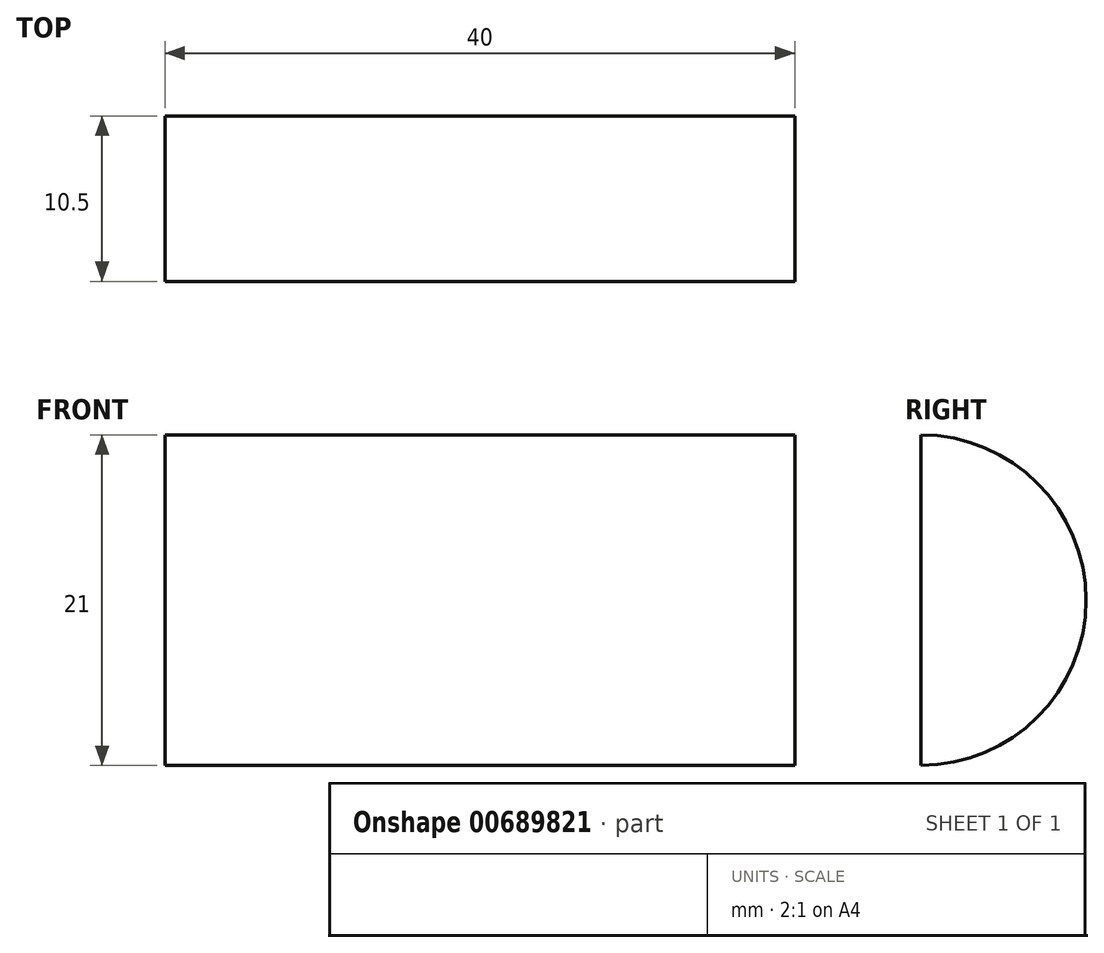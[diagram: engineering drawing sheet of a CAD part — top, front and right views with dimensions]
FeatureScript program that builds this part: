
annotation { "Feature Type Name" : "Feature", "Feature Type Description" : "" }
export const myFeature = defineFeature(function(context is Context, id is Id, definition is map)
    precondition{}
    {
        {
            var Q0;
            Q0=qCreatedBy(makeId("Front.planeOp"),FACE);
            var sketch = newSketch(context, id + "F0", { "sketchPlane" : qUnion([Q0])});
            skLineSegment(sketch, "E0.bottom", {"start": v(0, 70) * mm, "end": v(40, 70) * mm});
            skLineSegment(sketch, "E0.top", {"start": v(0, 0) * mm, "end": v(40, 0) * mm});
            skLineSegment(sketch, "E0.left", {"start": v(0, 70) * mm, "end": v(0, 0) * mm});
            skLineSegment(sketch, "E0.right", {"start": v(40, 70) * mm, "end": v(40, 0) * mm});
            skLineSegment(sketch, "E1", {"start": v(20, 0) * mm, "end": v(20, 70) * mm, "construction": true});
            skLineSegment(sketch, "E2", {"start": v(0, 35) * mm, "end": v(40, 35) * mm, "construction": true});
            skCircle(sketch, "E3", {"center": v(20, 61) * mm, "radius": 5 * mm});
            skCircle(sketch, "E4", {"center": v(20, 9) * mm, "radius": 5 * mm});
            skLineSegment(sketch, "E5", {"start": v(0, 51) * mm, "end": v(40, 51) * mm, "construction": true});
            skLineSegment(sketch, "E6", {"start": v(0, 19) * mm, "end": v(40, 19) * mm, "construction": true});
            skCircle(sketch, "E7", {"center": v(6, 51) * mm, "radius": 1.5 * mm});
            skCircle(sketch, "E8", {"center": v(34, 51) * mm, "radius": 1.5 * mm});
            skCircle(sketch, "E9", {"center": v(6, 19) * mm, "radius": 1.5 * mm});
            skCircle(sketch, "E10", {"center": v(34, 19) * mm, "radius": 1.5 * mm});
            skSolve(sketch);
        }
        {
            var Q0;
            Q0=makeQuery(id+"F0.imprint","IMPRINT",FACE,{"disambiguationData":[TD([[makeQuery(id+"F0.imprint","IMPRINT",EDGE,{"derivedFrom":sQuery(id+"F0.wireOp",EDGE,"E0.bottom")}),-1.0]])]});
            extrude(context, id + "F1", {"entities" : qUnion([Q0]), "depth" : 12 * mm, "offsetDistance" : 25 * mm});
        }
        {
            var Q0;
            Q0=makeQuery(id+"F1.opExtrude","SWEPT_FACE",FACE,{"disambiguationData":[OSD([sQuery(id+"F0.wireOp",EDGE,"E0.right")])]});
            var sketch = newSketch(context, id + "F2", { "sketchPlane" : qUnion([Q0])});
            skLineSegment(sketch, "E11", {"start": v(-12, 35) * mm, "end": v(0, 35) * mm, "construction": true});
            skArc(sketch, "E12", {"start": v(-12, 45.5) * mm, "mid": v(-1.5, 35) * mm, "end": v(-12, 24.5) * mm});
            skSolve(sketch);
        }
        {
            var Q0;
            {var subQ0=sQuery(id+"F2.wireOp",EDGE,"E12");Q0=makeQuery(id+"F2.imprint","IMPRINT",FACE,{"disambiguationData":[TD([[makeQuery(id+"F2.imprint","IMPRINT",EDGE,{"derivedFrom":subQ0}),-1.0]])]});}
            extrude(context, id + "F3", {"entities" : qUnion([Q0]), "operationType" : NewBodyOperationType.REMOVE, "endBound" : BoundingType.THROUGH_ALL, "oppositeDirection" : true, "depth" : 25 * mm, "offsetDistance" : 25 * mm});
        }
    });
